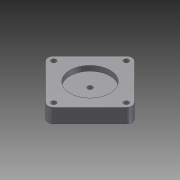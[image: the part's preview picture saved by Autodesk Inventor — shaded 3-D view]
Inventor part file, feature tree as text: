
AUTODESK INVENTOR PART (.ipt)
format: ipt  version: 2011 SP2 (Build 150309200, 309)  size: 115,200 bytes
history: native  units: mm
features: sketch x2, extrude x2, hole x1
ambient origin geometry x8: Origin, YZ Plane, XZ Plane, XY Plane, X Axis, Y Axis, Z Axis, Center Point
bodies: Solid1 (feature_tree)
feature tree (5):
  sketch  "Sketch1"  dims[d0=4.0mm d1=4.0mm]
  extrude  "Extrusion1"  Depth=4.0mm
  extrude  "Extrusion2"  Depth=10.0mm TaperAngle=0.0deg
  hole  "Hole1"  [1 undecoded]
  sketch  "Sketch2"  dims[d2=25.4mm d6=10.0mm d14=0.0mm d15=3.4mm d16=6.0mm d17=6.3mm d18=3.0mm d19=90.0deg d20=8.0mm d21=20.594885mm d22=20.05264mm d23=4.0mm d24=3.0mm d25=0.0mm]
note: 1 required parameter value undecoded (feature->parameter linkage not recoverable at this tier; creation-order binding heuristic only, values carry confidence <= 0.55)
